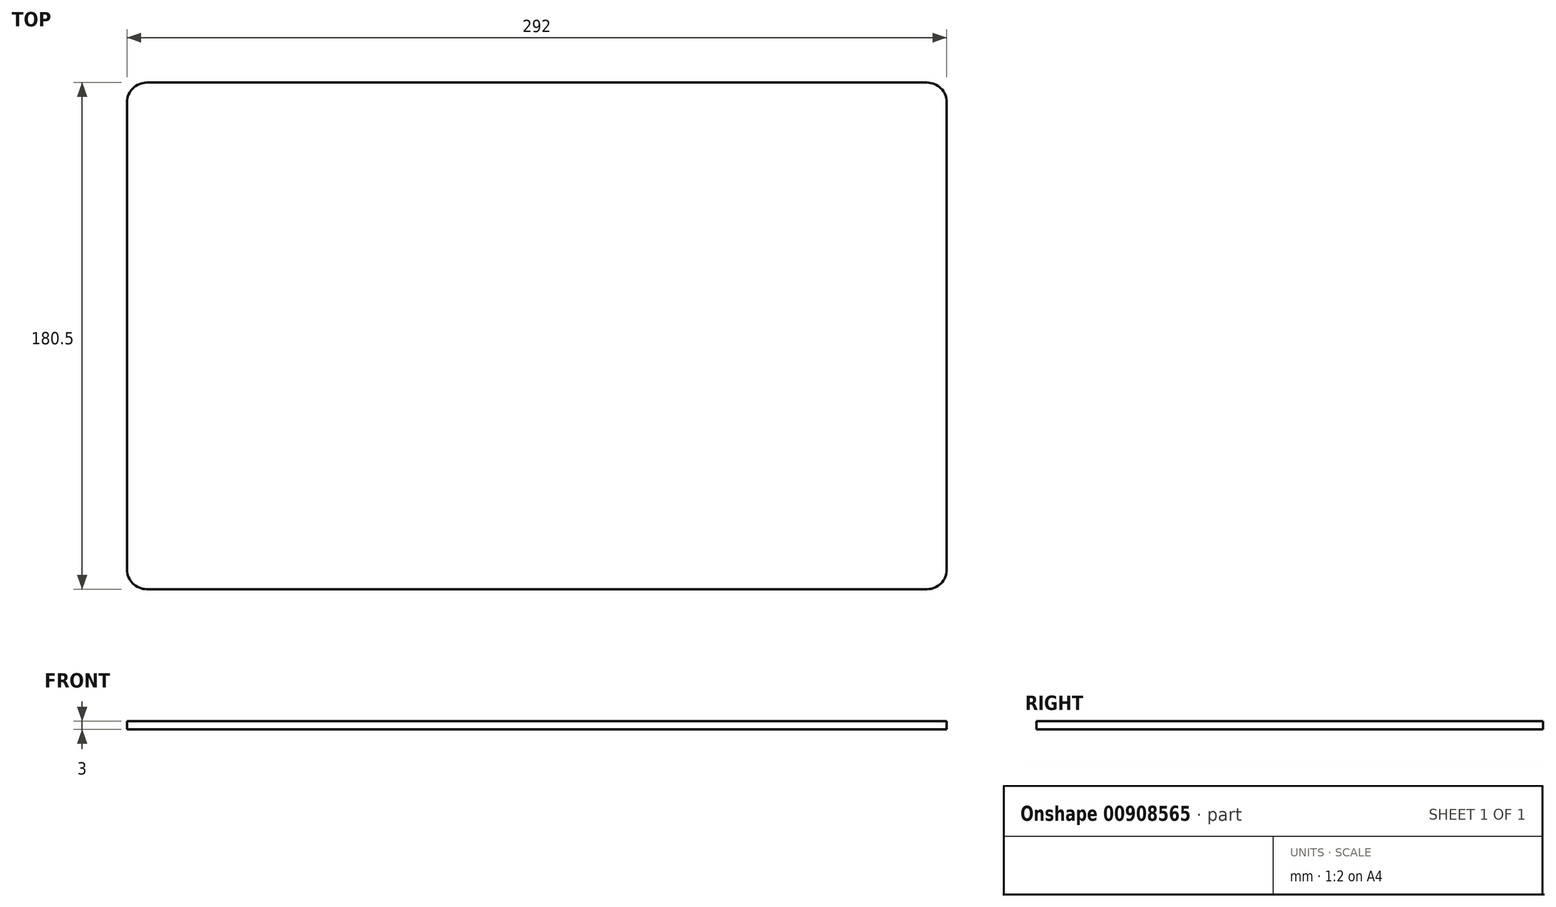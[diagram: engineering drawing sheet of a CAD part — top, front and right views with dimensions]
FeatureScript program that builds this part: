
annotation { "Feature Type Name" : "Feature", "Feature Type Description" : "" }
export const myFeature = defineFeature(function(context is Context, id is Id, definition is map)
    precondition{}
    {
        {
            var Q0;
            Q0=qCreatedBy(makeId("Top.planeOp"),FACE);
            var sketch = newSketch(context, id + "F0", { "sketchPlane" : qUnion([Q0])});
            skLineSegment(sketch, "E0.top", {"start": v(-139, -14.5) * mm, "end": v(139, -14.5) * mm});
            skPoint(sketch, "E0.middle", {"position": v(0, 0) * mm});
            skLineSegment(sketch, "E1", {"start": v(146, -14.5) * mm, "end": v(197.7, -14.5) * mm, "construction": true});
            skLineSegment(sketch, "E2", {"start": v(197.7, 166) * mm, "end": v(197.7, -14.5) * mm, "construction": true});
            skLineSegment(sketch, "E3.bottom", {"start": v(-139, 166) * mm, "end": v(139, 166) * mm});
            skLineSegment(sketch, "E4", {"start": v(197.7, 166) * mm, "end": v(146, 166) * mm, "construction": true});
            skLineSegment(sketch, "E5", {"start": v(-146, 159) * mm, "end": v(-146, -7.5) * mm});
            skLineSegment(sketch, "E6", {"start": v(146, -7.5) * mm, "end": v(146, 159) * mm});
            skLineSegment(sketch, "E7", {"start": v(-146, 141) * mm, "end": v(146, 141) * mm});
            skLineSegment(sketch, "E8", {"start": v(-43.28, 141) * mm, "end": v(-43.28, 166) * mm, "construction": true});
            skLineSegment(sketch, "E9", {"start": v(-146, 116) * mm, "end": v(146, 116) * mm});
            skLineSegment(sketch, "E10", {"start": v(146, 91) * mm, "end": v(-146, 91) * mm});
            skLineSegment(sketch, "E11", {"start": v(146, 66) * mm, "end": v(-146, 66) * mm});
            skLineSegment(sketch, "E12", {"start": v(146, 41) * mm, "end": v(-146, 41) * mm});
            skLineSegment(sketch, "E13", {"start": v(146, 16) * mm, "end": v(-146, 16) * mm});
            skLineSegment(sketch, "E14", {"start": v(-63.2, 141) * mm, "end": v(-63.2, 116) * mm, "construction": true});
            skLineSegment(sketch, "E15", {"start": v(-63.2, 116) * mm, "end": v(-63.2, 91) * mm, "construction": true});
            skLineSegment(sketch, "E16", {"start": v(-63.2, 91) * mm, "end": v(-63.2, 66) * mm, "construction": true});
            skLineSegment(sketch, "E17", {"start": v(-63.2, 66) * mm, "end": v(-63.2, 41) * mm, "construction": true});
            skLineSegment(sketch, "E18", {"start": v(-63.2, 41) * mm, "end": v(-63.2, 16) * mm, "construction": true});
            skLineSegment(sketch, "E19", {"start": v(146, 1) * mm, "end": v(-146, 1) * mm});
            skLineSegment(sketch, "E20", {"start": v(-63.2, 16) * mm, "end": v(-63.2, 1) * mm, "construction": true});
            skPoint(sketch, "E21.visualSharp", {"position": v(-146, -14.5) * mm});
            skArc(sketch, "E21.filletArc", {"start": v(-146, -7.5) * mm, "mid": v(-143.95, -12.45) * mm, "end": v(-139, -14.5) * mm});
            skPoint(sketch, "E22.visualSharp", {"position": v(146, -14.5) * mm});
            skArc(sketch, "E22.filletArc", {"start": v(139, -14.5) * mm, "mid": v(143.95, -12.45) * mm, "end": v(146, -7.5) * mm});
            skPoint(sketch, "E23.visualSharp", {"position": v(-146, 166) * mm});
            skArc(sketch, "E23.filletArc", {"start": v(-139, 166) * mm, "mid": v(-143.95, 163.95) * mm, "end": v(-146, 159) * mm});
            skPoint(sketch, "E24.visualSharp", {"position": v(146, 166) * mm});
            skArc(sketch, "E24.filletArc", {"start": v(146, 159) * mm, "mid": v(143.95, 163.95) * mm, "end": v(139, 166) * mm});
            skLineSegment(sketch, "E25", {"start": v(0, 223.83) * mm, "end": v(292, 223.83) * mm});
            skLineSegment(sketch, "E26", {"start": v(0, 223.83) * mm, "end": v(0, 229.83) * mm});
            skLineSegment(sketch, "E27", {"start": v(0, 229.83) * mm, "end": v(29.2, 229.83) * mm});
            skLineSegment(sketch, "E28", {"start": v(29.2, 229.83) * mm, "end": v(29.2, 223.83) * mm});
            skLineSegment(sketch, "E29", {"start": v(58.4, 223.83) * mm, "end": v(58.4, 229.83) * mm});
            skLineSegment(sketch, "E30", {"start": v(58.4, 229.83) * mm, "end": v(87.6, 229.83) * mm});
            skLineSegment(sketch, "E31", {"start": v(87.6, 229.83) * mm, "end": v(87.6, 223.83) * mm});
            skLineSegment(sketch, "E32", {"start": v(29.2, 229.83) * mm, "end": v(58.4, 229.83) * mm, "construction": true});
            skLineSegment(sketch, "E33", {"start": v(87.6, 229.83) * mm, "end": v(116.8, 229.83) * mm, "construction": true});
            skLineSegment(sketch, "E34", {"start": v(116.8, 229.83) * mm, "end": v(116.8, 223.83) * mm});
            skLineSegment(sketch, "E35", {"start": v(116.8, 229.83) * mm, "end": v(146, 229.83) * mm});
            skLineSegment(sketch, "E36", {"start": v(146, 229.83) * mm, "end": v(146, 223.83) * mm});
            skLineSegment(sketch, "E37", {"start": v(146, 223.83) * mm, "end": v(146, 229.83) * mm});
            skLineSegment(sketch, "E38", {"start": v(175.2, 229.83) * mm, "end": v(175.2, 223.83) * mm});
            skLineSegment(sketch, "E39", {"start": v(175.2, 229.83) * mm, "end": v(204.4, 229.83) * mm});
            skLineSegment(sketch, "E40", {"start": v(204.4, 229.83) * mm, "end": v(204.4, 223.83) * mm});
            skLineSegment(sketch, "E41", {"start": v(146, 229.83) * mm, "end": v(175.2, 229.83) * mm, "construction": true});
            skLineSegment(sketch, "E42", {"start": v(204.4, 229.83) * mm, "end": v(233.6, 229.83) * mm, "construction": true});
            skLineSegment(sketch, "E43", {"start": v(233.6, 223.83) * mm, "end": v(233.6, 229.83) * mm});
            skLineSegment(sketch, "E44", {"start": v(262.8, 229.83) * mm, "end": v(262.8, 223.83) * mm});
            skLineSegment(sketch, "E45", {"start": v(233.6, 229.83) * mm, "end": v(262.8, 229.83) * mm});
            skPoint(sketch, "E46.visualSharp", {"position": v(-461.84, 249.97) * mm});
            skLineSegment(sketch, "E47", {"start": v(-642.62, 391.26) * mm, "end": v(-350.62, 391.26) * mm});
            skLineSegment(sketch, "E48", {"start": v(-642.62, 391.26) * mm, "end": v(-642.62, 397.26) * mm});
            skLineSegment(sketch, "E49", {"start": v(-642.62, 397.26) * mm, "end": v(-613.42, 397.26) * mm});
            skLineSegment(sketch, "E50", {"start": v(-613.42, 397.26) * mm, "end": v(-613.42, 391.26) * mm});
            skLineSegment(sketch, "E51", {"start": v(-584.22, 391.26) * mm, "end": v(-584.22, 397.26) * mm});
            skLineSegment(sketch, "E52", {"start": v(-584.22, 397.26) * mm, "end": v(-555.02, 397.26) * mm});
            skLineSegment(sketch, "E53", {"start": v(-555.02, 397.26) * mm, "end": v(-555.02, 391.26) * mm});
            skLineSegment(sketch, "E54", {"start": v(-613.42, 397.26) * mm, "end": v(-584.22, 397.26) * mm, "construction": true});
            skLineSegment(sketch, "E55", {"start": v(-555.02, 397.26) * mm, "end": v(-525.82, 397.26) * mm, "construction": true});
            skLineSegment(sketch, "E56", {"start": v(-525.82, 397.26) * mm, "end": v(-525.82, 391.26) * mm});
            skLineSegment(sketch, "E57", {"start": v(-525.82, 397.26) * mm, "end": v(-496.62, 397.26) * mm});
            skLineSegment(sketch, "E58", {"start": v(-496.62, 397.26) * mm, "end": v(-496.62, 391.26) * mm});
            skLineSegment(sketch, "E59", {"start": v(-496.62, 391.26) * mm, "end": v(-496.62, 397.26) * mm});
            skLineSegment(sketch, "E60", {"start": v(-467.42, 397.26) * mm, "end": v(-467.42, 391.26) * mm});
            skLineSegment(sketch, "E61", {"start": v(-467.42, 397.26) * mm, "end": v(-438.22, 397.26) * mm});
            skLineSegment(sketch, "E62", {"start": v(-438.22, 397.26) * mm, "end": v(-438.22, 391.26) * mm});
            skLineSegment(sketch, "E63", {"start": v(-496.62, 397.26) * mm, "end": v(-467.42, 397.26) * mm, "construction": true});
            skLineSegment(sketch, "E64", {"start": v(-438.22, 397.26) * mm, "end": v(-409.02, 397.26) * mm, "construction": true});
            skLineSegment(sketch, "E65", {"start": v(-409.02, 391.26) * mm, "end": v(-409.02, 397.26) * mm});
            skLineSegment(sketch, "E66", {"start": v(-379.82, 397.26) * mm, "end": v(-379.82, 391.26) * mm});
            skLineSegment(sketch, "E67", {"start": v(-409.02, 397.26) * mm, "end": v(-379.82, 397.26) * mm});
            skPoint(sketch, "E68.visualSharp", {"position": v(-528.27, 599.49) * mm});
            skLineSegment(sketch, "E69", {"start": v(-350.45, 378.26) * mm, "end": v(-642.45, 378.26) * mm});
            skLineSegment(sketch, "E70", {"start": v(-350.45, 378.26) * mm, "end": v(-350.45, 372.26) * mm});
            skLineSegment(sketch, "E71", {"start": v(-350.45, 372.26) * mm, "end": v(-379.65, 372.26) * mm});
            skLineSegment(sketch, "E72", {"start": v(-379.65, 372.26) * mm, "end": v(-379.65, 378.26) * mm});
            skLineSegment(sketch, "E73", {"start": v(-408.85, 378.26) * mm, "end": v(-408.85, 372.26) * mm});
            skLineSegment(sketch, "E74", {"start": v(-408.85, 372.26) * mm, "end": v(-438.05, 372.26) * mm});
            skLineSegment(sketch, "E75", {"start": v(-438.05, 372.26) * mm, "end": v(-438.05, 378.26) * mm});
            skLineSegment(sketch, "E76", {"start": v(-379.65, 372.26) * mm, "end": v(-408.85, 372.26) * mm, "construction": true});
            skLineSegment(sketch, "E77", {"start": v(-438.05, 372.26) * mm, "end": v(-467.25, 372.26) * mm, "construction": true});
            skLineSegment(sketch, "E78", {"start": v(-467.25, 372.26) * mm, "end": v(-467.25, 378.26) * mm});
            skLineSegment(sketch, "E79", {"start": v(-467.25, 372.26) * mm, "end": v(-496.45, 372.26) * mm});
            skLineSegment(sketch, "E80", {"start": v(-496.45, 372.26) * mm, "end": v(-496.45, 378.26) * mm});
            skLineSegment(sketch, "E81", {"start": v(-496.45, 378.26) * mm, "end": v(-496.45, 372.26) * mm});
            skLineSegment(sketch, "E82", {"start": v(-525.65, 372.26) * mm, "end": v(-525.65, 378.26) * mm});
            skLineSegment(sketch, "E83", {"start": v(-525.65, 372.26) * mm, "end": v(-554.85, 372.26) * mm});
            skLineSegment(sketch, "E84", {"start": v(-554.85, 372.26) * mm, "end": v(-554.85, 378.26) * mm});
            skLineSegment(sketch, "E85", {"start": v(-496.45, 372.26) * mm, "end": v(-525.65, 372.26) * mm, "construction": true});
            skLineSegment(sketch, "E86", {"start": v(-554.85, 372.26) * mm, "end": v(-584.05, 372.26) * mm, "construction": true});
            skLineSegment(sketch, "E87", {"start": v(-584.05, 378.26) * mm, "end": v(-584.05, 372.26) * mm});
            skLineSegment(sketch, "E88", {"start": v(-613.25, 372.26) * mm, "end": v(-613.25, 378.26) * mm});
            skLineSegment(sketch, "E89", {"start": v(-584.05, 372.26) * mm, "end": v(-613.25, 372.26) * mm});
            skLineSegment(sketch, "E90", {"start": v(-642.62, 391.26) * mm, "end": v(-642.45, 378.26) * mm});
            skLineSegment(sketch, "E91", {"start": v(-350.62, 391.26) * mm, "end": v(-350.45, 378.26) * mm});
            skLineSegment(sketch, "E92", {"start": v(-647.96, 233.8) * mm, "end": v(-355.96, 233.8) * mm});
            skLineSegment(sketch, "E93", {"start": v(-647.96, 233.8) * mm, "end": v(-647.96, 239.8) * mm});
            skLineSegment(sketch, "E94", {"start": v(-647.96, 239.8) * mm, "end": v(-618.76, 239.8) * mm});
            skLineSegment(sketch, "E95", {"start": v(-618.76, 239.8) * mm, "end": v(-618.76, 233.8) * mm});
            skLineSegment(sketch, "E96", {"start": v(-589.56, 233.8) * mm, "end": v(-589.56, 239.8) * mm});
            skLineSegment(sketch, "E97", {"start": v(-589.56, 239.8) * mm, "end": v(-560.36, 239.8) * mm});
            skLineSegment(sketch, "E98", {"start": v(-560.36, 239.8) * mm, "end": v(-560.36, 233.8) * mm});
            skLineSegment(sketch, "E99", {"start": v(-618.76, 239.8) * mm, "end": v(-589.56, 239.8) * mm, "construction": true});
            skLineSegment(sketch, "E100", {"start": v(-560.36, 239.8) * mm, "end": v(-531.16, 239.8) * mm, "construction": true});
            skLineSegment(sketch, "E101", {"start": v(-531.16, 239.8) * mm, "end": v(-531.16, 233.8) * mm});
            skLineSegment(sketch, "E102", {"start": v(-531.16, 239.8) * mm, "end": v(-501.96, 239.8) * mm});
            skLineSegment(sketch, "E103", {"start": v(-501.96, 239.8) * mm, "end": v(-501.96, 233.8) * mm});
            skLineSegment(sketch, "E104", {"start": v(-501.96, 233.8) * mm, "end": v(-501.96, 239.8) * mm});
            skLineSegment(sketch, "E105", {"start": v(-472.76, 239.8) * mm, "end": v(-472.76, 233.8) * mm});
            skLineSegment(sketch, "E106", {"start": v(-472.76, 239.8) * mm, "end": v(-443.56, 239.8) * mm});
            skLineSegment(sketch, "E107", {"start": v(-443.56, 239.8) * mm, "end": v(-443.56, 233.8) * mm});
            skLineSegment(sketch, "E108", {"start": v(-501.96, 239.8) * mm, "end": v(-472.76, 239.8) * mm, "construction": true});
            skLineSegment(sketch, "E109", {"start": v(-443.56, 239.8) * mm, "end": v(-414.36, 239.8) * mm, "construction": true});
            skLineSegment(sketch, "E110", {"start": v(-414.36, 233.8) * mm, "end": v(-414.36, 239.8) * mm});
            skLineSegment(sketch, "E111", {"start": v(-385.16, 239.8) * mm, "end": v(-385.16, 233.8) * mm});
            skLineSegment(sketch, "E112", {"start": v(-414.36, 239.8) * mm, "end": v(-385.16, 239.8) * mm});
            skLineSegment(sketch, "E113", {"start": v(-355.92, 230.8) * mm, "end": v(-647.92, 230.8) * mm});
            skLineSegment(sketch, "E114", {"start": v(-355.92, 230.8) * mm, "end": v(-355.92, 224.8) * mm});
            skLineSegment(sketch, "E115", {"start": v(-355.92, 224.8) * mm, "end": v(-385.12, 224.8) * mm});
            skLineSegment(sketch, "E116", {"start": v(-385.12, 224.8) * mm, "end": v(-385.12, 230.8) * mm});
            skLineSegment(sketch, "E117", {"start": v(-414.32, 230.8) * mm, "end": v(-414.32, 224.8) * mm});
            skLineSegment(sketch, "E118", {"start": v(-414.32, 224.8) * mm, "end": v(-443.52, 224.8) * mm});
            skLineSegment(sketch, "E119", {"start": v(-443.52, 224.8) * mm, "end": v(-443.52, 230.8) * mm});
            skLineSegment(sketch, "E120", {"start": v(-385.12, 224.8) * mm, "end": v(-414.32, 224.8) * mm, "construction": true});
            skLineSegment(sketch, "E121", {"start": v(-443.52, 224.8) * mm, "end": v(-472.72, 224.8) * mm, "construction": true});
            skLineSegment(sketch, "E122", {"start": v(-472.72, 224.8) * mm, "end": v(-472.72, 230.8) * mm});
            skLineSegment(sketch, "E123", {"start": v(-472.72, 224.8) * mm, "end": v(-501.92, 224.8) * mm});
            skLineSegment(sketch, "E124", {"start": v(-501.92, 224.8) * mm, "end": v(-501.92, 230.8) * mm});
            skLineSegment(sketch, "E125", {"start": v(-501.92, 230.8) * mm, "end": v(-501.92, 224.8) * mm});
            skLineSegment(sketch, "E126", {"start": v(-531.12, 224.8) * mm, "end": v(-531.12, 230.8) * mm});
            skLineSegment(sketch, "E127", {"start": v(-531.12, 224.8) * mm, "end": v(-560.32, 224.8) * mm});
            skLineSegment(sketch, "E128", {"start": v(-560.32, 224.8) * mm, "end": v(-560.32, 230.8) * mm});
            skLineSegment(sketch, "E129", {"start": v(-501.92, 224.8) * mm, "end": v(-531.12, 224.8) * mm, "construction": true});
            skLineSegment(sketch, "E130", {"start": v(-560.32, 224.8) * mm, "end": v(-589.52, 224.8) * mm, "construction": true});
            skLineSegment(sketch, "E131", {"start": v(-589.52, 230.8) * mm, "end": v(-589.52, 224.8) * mm});
            skLineSegment(sketch, "E132", {"start": v(-618.72, 224.8) * mm, "end": v(-618.72, 230.8) * mm});
            skLineSegment(sketch, "E133", {"start": v(-589.52, 224.8) * mm, "end": v(-618.72, 224.8) * mm});
            skLineSegment(sketch, "E134", {"start": v(-647.96, 233.8) * mm, "end": v(-647.92, 230.8) * mm});
            skLineSegment(sketch, "E135", {"start": v(-355.96, 233.8) * mm, "end": v(-355.92, 230.8) * mm});
            skLineSegment(sketch, "E136", {"start": v(-646.53, 172.01) * mm, "end": v(-354.53, 172.01) * mm});
            skLineSegment(sketch, "E137", {"start": v(-646.53, 172.01) * mm, "end": v(-646.53, 178.01) * mm});
            skLineSegment(sketch, "E138", {"start": v(-646.53, 178.01) * mm, "end": v(-617.33, 178.01) * mm});
            skLineSegment(sketch, "E139", {"start": v(-617.33, 178.01) * mm, "end": v(-617.33, 172.01) * mm});
            skLineSegment(sketch, "E140", {"start": v(-588.13, 172.01) * mm, "end": v(-588.13, 178.01) * mm});
            skLineSegment(sketch, "E141", {"start": v(-588.13, 178.01) * mm, "end": v(-558.93, 178.01) * mm});
            skLineSegment(sketch, "E142", {"start": v(-558.93, 178.01) * mm, "end": v(-558.93, 172.01) * mm});
            skLineSegment(sketch, "E143", {"start": v(-617.33, 178.01) * mm, "end": v(-588.13, 178.01) * mm, "construction": true});
            skLineSegment(sketch, "E144", {"start": v(-558.93, 178.01) * mm, "end": v(-529.73, 178.01) * mm, "construction": true});
            skLineSegment(sketch, "E145", {"start": v(-529.73, 178.01) * mm, "end": v(-529.73, 172.01) * mm});
            skLineSegment(sketch, "E146", {"start": v(-529.73, 178.01) * mm, "end": v(-500.53, 178.01) * mm});
            skLineSegment(sketch, "E147", {"start": v(-500.53, 178.01) * mm, "end": v(-500.53, 172.01) * mm});
            skLineSegment(sketch, "E148", {"start": v(-500.53, 172.01) * mm, "end": v(-500.53, 178.01) * mm});
            skLineSegment(sketch, "E149", {"start": v(-471.33, 178.01) * mm, "end": v(-471.33, 172.01) * mm});
            skLineSegment(sketch, "E150", {"start": v(-471.33, 178.01) * mm, "end": v(-442.13, 178.01) * mm});
            skLineSegment(sketch, "E151", {"start": v(-442.13, 178.01) * mm, "end": v(-442.13, 172.01) * mm});
            skLineSegment(sketch, "E152", {"start": v(-500.53, 178.01) * mm, "end": v(-471.33, 178.01) * mm, "construction": true});
            skLineSegment(sketch, "E153", {"start": v(-442.13, 178.01) * mm, "end": v(-412.93, 178.01) * mm, "construction": true});
            skLineSegment(sketch, "E154", {"start": v(-412.93, 172.01) * mm, "end": v(-412.93, 178.01) * mm});
            skLineSegment(sketch, "E155", {"start": v(-383.73, 178.01) * mm, "end": v(-383.73, 172.01) * mm});
            skLineSegment(sketch, "E156", {"start": v(-412.93, 178.01) * mm, "end": v(-383.73, 178.01) * mm});
            skLineSegment(sketch, "E157", {"start": v(-646.53, 172.01) * mm, "end": v(-646.53, 170.01) * mm});
            skLineSegment(sketch, "E158", {"start": v(-639.53, 163.01) * mm, "end": v(-361.53, 163.01) * mm});
            skLineSegment(sketch, "E159", {"start": v(-354.53, 170.01) * mm, "end": v(-354.53, 172.01) * mm});
            skPoint(sketch, "E160.visualSharp", {"position": v(-354.53, 163.01) * mm});
            skArc(sketch, "E160.filletArc", {"start": v(-361.53, 163.01) * mm, "mid": v(-356.58, 165.06) * mm, "end": v(-354.53, 170.01) * mm});
            skPoint(sketch, "E161.visualSharp", {"position": v(-646.53, 163.01) * mm});
            skArc(sketch, "E161.filletArc", {"start": v(-646.53, 170.01) * mm, "mid": v(-644.48, 165.06) * mm, "end": v(-639.53, 163.01) * mm});
            skLineSegment(sketch, "E162", {"start": v(-350.32, 486.14) * mm, "end": v(-642.32, 486.14) * mm});
            skLineSegment(sketch, "E163", {"start": v(-350.32, 486.14) * mm, "end": v(-350.32, 480.14) * mm});
            skLineSegment(sketch, "E164", {"start": v(-350.32, 480.14) * mm, "end": v(-379.52, 480.14) * mm});
            skLineSegment(sketch, "E165", {"start": v(-379.52, 480.14) * mm, "end": v(-379.52, 486.14) * mm});
            skLineSegment(sketch, "E166", {"start": v(-408.72, 486.14) * mm, "end": v(-408.72, 480.14) * mm});
            skLineSegment(sketch, "E167", {"start": v(-408.72, 480.14) * mm, "end": v(-437.92, 480.14) * mm});
            skLineSegment(sketch, "E168", {"start": v(-437.92, 480.14) * mm, "end": v(-437.92, 486.14) * mm});
            skLineSegment(sketch, "E169", {"start": v(-379.52, 480.14) * mm, "end": v(-408.72, 480.14) * mm, "construction": true});
            skLineSegment(sketch, "E170", {"start": v(-437.92, 480.14) * mm, "end": v(-467.12, 480.14) * mm, "construction": true});
            skLineSegment(sketch, "E171", {"start": v(-467.12, 480.14) * mm, "end": v(-467.12, 486.14) * mm});
            skLineSegment(sketch, "E172", {"start": v(-467.12, 480.14) * mm, "end": v(-496.32, 480.14) * mm});
            skLineSegment(sketch, "E173", {"start": v(-496.32, 480.14) * mm, "end": v(-496.32, 486.14) * mm});
            skLineSegment(sketch, "E174", {"start": v(-496.32, 486.14) * mm, "end": v(-496.32, 480.14) * mm});
            skLineSegment(sketch, "E175", {"start": v(-525.52, 480.14) * mm, "end": v(-525.52, 486.14) * mm});
            skLineSegment(sketch, "E176", {"start": v(-525.52, 480.14) * mm, "end": v(-554.72, 480.14) * mm});
            skLineSegment(sketch, "E177", {"start": v(-554.72, 480.14) * mm, "end": v(-554.72, 486.14) * mm});
            skLineSegment(sketch, "E178", {"start": v(-496.32, 480.14) * mm, "end": v(-525.52, 480.14) * mm, "construction": true});
            skLineSegment(sketch, "E179", {"start": v(-554.72, 480.14) * mm, "end": v(-583.92, 480.14) * mm, "construction": true});
            skLineSegment(sketch, "E180", {"start": v(-583.92, 486.14) * mm, "end": v(-583.92, 480.14) * mm});
            skLineSegment(sketch, "E181", {"start": v(-613.12, 480.14) * mm, "end": v(-613.12, 486.14) * mm});
            skLineSegment(sketch, "E182", {"start": v(-583.92, 480.14) * mm, "end": v(-613.12, 480.14) * mm});
            skLineSegment(sketch, "E183", {"start": v(-642.32, 486.14) * mm, "end": v(-642.32, 498.14) * mm});
            skLineSegment(sketch, "E184", {"start": v(-635.32, 505.14) * mm, "end": v(-357.32, 505.14) * mm});
            skLineSegment(sketch, "E185", {"start": v(-350.32, 498.14) * mm, "end": v(-350.32, 486.14) * mm});
            skPoint(sketch, "E186.visualSharp", {"position": v(-642.32, 505.14) * mm});
            skArc(sketch, "E186.filletArc", {"start": v(-635.32, 505.14) * mm, "mid": v(-640.27, 503.09) * mm, "end": v(-642.32, 498.14) * mm});
            skPoint(sketch, "E187.visualSharp", {"position": v(-350.32, 505.14) * mm});
            skArc(sketch, "E187.filletArc", {"start": v(-350.32, 498.14) * mm, "mid": v(-352.37, 503.09) * mm, "end": v(-357.32, 505.14) * mm});
            skSolve(sketch);
        }
        {
            var Q0;
            Q0=makeQuery(id+"F0.imprint","IMPRINT",FACE,{"disambiguationData":[TD([[makeQuery(id+"F0.imprint","IMPRINT",EDGE,{"derivedFrom":sQuery(id+"F0.wireOp",EDGE,"E3.bottom")}),-1.0]])]});
            var Q1;
            {var subQ0=sQuery(id+"F0.wireOp",EDGE,"E7");Q1=makeQuery(id+"F0.imprint","IMPRINT",FACE,{"disambiguationData":[TD([[makeQuery(id+"F0.imprint","IMPRINT",EDGE,{"derivedFrom":subQ0}),-1.0]])]});}
            var Q2;
            {var subQ0=sQuery(id+"F0.wireOp",EDGE,"E9");Q2=makeQuery(id+"F0.imprint","IMPRINT",FACE,{"disambiguationData":[TD([[makeQuery(id+"F0.imprint","IMPRINT",EDGE,{"derivedFrom":subQ0}),-1.0]])]});}
            var Q3;
            {var subQ0=sQuery(id+"F0.wireOp",EDGE,"E10");Q3=makeQuery(id+"F0.imprint","IMPRINT",FACE,{"disambiguationData":[TD([[makeQuery(id+"F0.imprint","IMPRINT",EDGE,{"derivedFrom":subQ0}),1.0]])]});}
            var Q4;
            {var subQ0=sQuery(id+"F0.wireOp",EDGE,"E11");Q4=makeQuery(id+"F0.imprint","IMPRINT",FACE,{"disambiguationData":[TD([[makeQuery(id+"F0.imprint","IMPRINT",EDGE,{"derivedFrom":subQ0}),1.0]])]});}
            var Q5;
            {var subQ0=sQuery(id+"F0.wireOp",EDGE,"E12");Q5=makeQuery(id+"F0.imprint","IMPRINT",FACE,{"disambiguationData":[TD([[makeQuery(id+"F0.imprint","IMPRINT",EDGE,{"derivedFrom":subQ0}),1.0]])]});}
            var Q6;
            {var subQ0=sQuery(id+"F0.wireOp",EDGE,"E13");Q6=makeQuery(id+"F0.imprint","IMPRINT",FACE,{"disambiguationData":[TD([[makeQuery(id+"F0.imprint","IMPRINT",EDGE,{"derivedFrom":subQ0}),1.0]])]});}
            var Q7;
            Q7=makeQuery(id+"F0.imprint","IMPRINT",FACE,{"disambiguationData":[TD([[makeQuery(id+"F0.imprint","IMPRINT",EDGE,{"derivedFrom":sQuery(id+"F0.wireOp",EDGE,"E0.top")}),1.0]])]});
            extrude(context, id + "F1", {"entities" : qUnion([Q0, Q1, Q2, Q3, Q4, Q5, Q6, Q7]), "depth" : 3 * mm, "offsetDistance" : 25 * mm});
        }
    });
